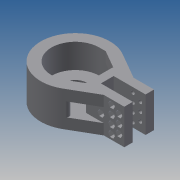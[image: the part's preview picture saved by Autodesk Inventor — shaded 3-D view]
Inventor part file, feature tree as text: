
AUTODESK INVENTOR PART (.ipt)
format: ipt  version: 2013 (Build 170138000, 138)  size: 413,696 bytes
history: native  units: mm
features: extrude x16, sketch x16, fillet x2, mirror x1, pattern_circular x1, projected_geometry x1
ambient origin geometry x8: Origin, YZ Plane, XZ Plane, XY Plane, X Axis, Y Axis, Z Axis, Center Point
bodies: Solid1 (feature_tree)
feature tree (37):
  extrude  "Extrusion1"  Depth=112.5mm
  extrude  "Extrusion2"  Depth=65.0mm
  extrude  "Extrusion3"  Depth=45.0mm
  extrude  "Extrusion4"  Depth=23.0mm TaperAngle=0.0deg
  extrude  "Extrusion5"  Depth=13.0mm TaperAngle=0.0deg
  extrude  "Extrusion6"  Depth=13.0mm TaperAngle=0.0deg
  extrude  "Extrusion7"  Depth=2.5mm
  mirror  "Mirror1"
  fillet  "Fillet1"  Radius=22.0mm
  extrude  "Extrusion8"  Depth=15.0mm
  extrude  "Extrusion9"  Depth=3.5mm
  fillet  "Fillet2"  Radius=40.0mm
  extrude  "Extrusion10"  Depth=10.0mm TaperAngle=0.0deg
  extrude  "Extrusion11"  Depth=30.0mm
  extrude  "Extrusion12"  Depth=10.0mm TaperAngle=0.0deg
  extrude  "Extrusion13"  Depth=3.5mm
  extrude  "Extrusion14"  Depth=7.0mm
  extrude  "Extrusion15"  Depth=6.0mm
  extrude  "Extrusion16"  Depth=5.5mm
  pattern_circular  "Circular Pattern1"  [2 undecoded]
  sketch  "Sketch1"  dims[d0=28.0mm d2=112.5mm]
  sketch  "Sketch2"  dims[d3=33.0mm d4=0.0mm d5=65.0mm]
  sketch  "Sketch3"  dims[d7=33.0mm d8=0.0mm d10=45.0mm]
  sketch  "Sketch4"  dims[d12=23.0mm d13=0.0mm d14=23.0mm d15=0.0mm]
  sketch  "Sketch5"  dims[d16=60.0deg d17=13.0mm d18=0.0mm]
  projected_geometry  "Projected Loop1"
  sketch  "Sketch6"  dims[d19=10.0mm d20=13.0mm d21=0.0mm]
  sketch  "Sketch7"  dims[d22=13.0mm d23=0.0mm d24=2.5mm d25=22.0mm]
  sketch  "Sketch8"  dims[d27=7.0mm d28=0.0mm d29=15.0mm]
  sketch  "Sketch9"  dims[d31=7.0mm d32=0.0mm d33=3.5mm d34=40.0mm]
  sketch  "Sketch10"  dims[d35=12.0mm d36=10.0mm d37=0.0mm]
  sketch  "Sketch11"  dims[d38=8.0mm d39=30.0mm]
  sketch  "Sketch12"  dims[d40=45.0mm d41=10.0mm d42=0.0mm]
  sketch  "Sketch13"  dims[d43=8.0mm d45=3.5mm]
  sketch  "Sketch14"  dims[d47=5.0mm d48=7.0mm]
  sketch  "Sketch17"  dims[d49=10.0mm d50=0.0mm d51=6.0mm]
  sketch  "Sketch18"  dims[d53=3.0mm d54=0.0mm d55=5.5mm d56=4.0mm d57=0.0mm d59=8.0mm d60=3.5mm d62=17.5mm d63=10.0mm d64=0.0mm d65=5.5mm d66=4.0mm d67=0.0mm d68=40.0mm d69=360.0deg]
note: 2 required parameter values undecoded (feature->parameter linkage not recoverable at this tier; creation-order binding heuristic only, values carry confidence <= 0.55)
